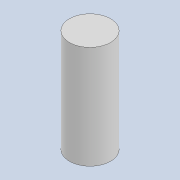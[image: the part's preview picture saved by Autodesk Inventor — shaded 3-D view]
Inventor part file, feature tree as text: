
AUTODESK INVENTOR PART (.ipt)
format: ipt  version: 2020 (Build 240168000, 168)  size: 72,192 bytes
history: native  units: mm
features: extrude x1, sketch x1
ambient origin geometry x8: Origin, YZ Plane, XZ Plane, XY Plane, X Axis, Y Axis, Z Axis, Center Point
bodies: Solid1 (feature_tree)
feature tree (2):
  extrude  "Extrusion1"  Depth=5.0mm TaperAngle=0.0deg
  sketch  "Sketch1"  dims[d0=2.0mm d1=5.0mm d2=0.0mm]
